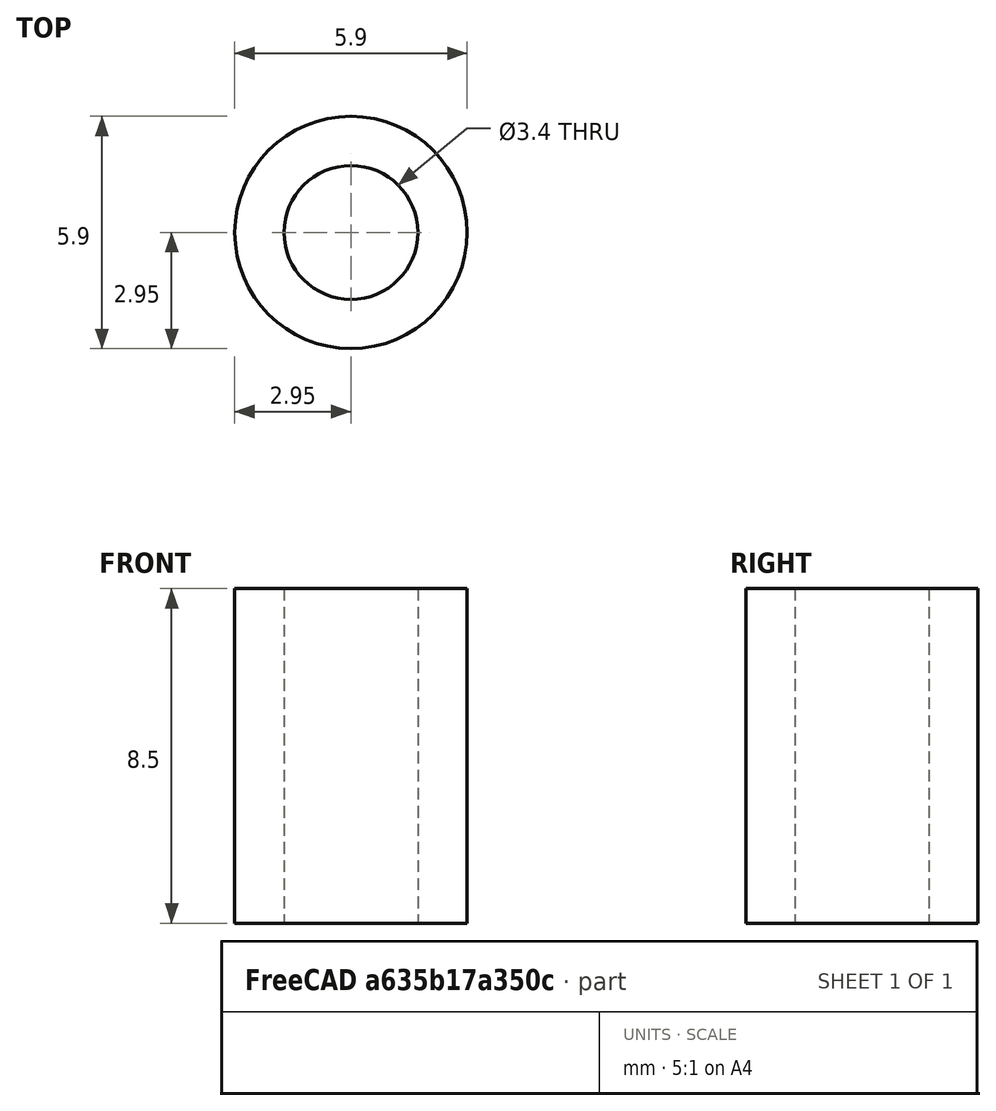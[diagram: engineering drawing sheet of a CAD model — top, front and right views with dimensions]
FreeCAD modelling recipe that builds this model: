
FCSTD DOCUMENT  (FreeCAD 2023.321R14555 (Git shallow))
Label: Spacer_9mm
License: All rights reserved
LicenseURL: http://en.wikipedia.org/wiki/All_rights_reserved
objects: Sketcher::SketchObject×1, PartDesign::Pad×1, PartDesign::Hole×1, PartDesign::Body×1, Mesh::Feature×1
note: 9 computed .brp shape members not serialized (recipe doc carries the construction recipe); baked Part::Feature solids carry a one-line shape summary decoded from their .brp

FEATURE [Sketcher::SketchObject] Sketch
  ArcFitTolerance = 1e-06
  AttachmentSupport = -> [XY_Plane]
  ExternalBSplineMaxDegree = 5
  ExternalBSplineTolerance = 0.0001
  FullyConstrained = false
  InternalTolerance = 1e-06
  InvalidShape = false
  MakeInternals = false
  MapMode = 5
  Support = -> [XY_Plane]
  TreeRank = 11
  ValidateShape = false
  sketch-geometry (1):
    g0: Circle CenterX=0 CenterY=0 CenterZ=0 NormalX=0 NormalY=0 NormalZ=1 AngleXU=0 Radius=2.9503
  constraints (1):
    c: Coincident(g0,g-1)
FEATURE [PartDesign::Pad] Pad
  AddSubType = 0
  AlongSketchNormal = false
  AutoTaperInnerAngle = true
  CheckUpToFaceLimits = true
  ClaimChildren = false
  Direction = (0,0,1)
  Fit = 0
  FitJoin = 0
  InnerFit = 0
  InnerFitJoin = 0
  InvalidShape = false
  Length = 8.5
  Length2 = 100
  Linearize = true
  NewSolid = false
  Profile = -> Sketch
  Suppress = false
  TaperInnerAngle = 0
  TaperInnerAngleRev = 0
  TreeRank = 12
  Type = 0
  ValidateShape = true
  _ProfileBasedVersion = 1
FEATURE [PartDesign::Hole] Hole
  AddSubType = 1
  BaseFeature = -> Pad
  ClaimChildren = false
  CustomThreadClearance = 0
  Depth = 25
  DepthType = 0
  Diameter = 3.4
  DrillForDepth = false
  DrillPoint = 1
  DrillPointAngle = 118
  Fit = 0
  FitJoin = 0
  HoleCutCountersinkAngle = 90
  HoleCutCustomValues = false
  HoleCutDepth = 0
  HoleCutDiameter = 6.1
  HoleCutType = 0
  InnerFit = 0
  InnerFitJoin = 0
  InvalidShape = false
  Linearize = true
  ModelThread = false
  NewSolid = false
  Profile = -> Pad [Face3]
  Suppress = false
  Tapered = false
  TaperedAngle = 90
  ThreadClass = 0
  ThreadDepth = 25
  ThreadDepthType = 0
  ThreadDirection = 0
  ThreadFit = 0
  ThreadSize = 9
  ThreadType = 1
  Threaded = false
  TreeRank = 13
  UseCustomThreadClearance = false
  ValidateShape = true
  _ProfileBasedVersion = 1
FEATURE [PartDesign::Body] Body
  AutoGroupSolids = false
  ClaimAllChildren = false
  ExportMode = 0
  Group = -> [Sketch,Pad,Hole]
  InvalidShape = false
  Origin = -> Origin
  Tip = -> Hole
  TreeRank = 10
  ValidateShape = false
  _ExportChildren = -> [Pad,Hole]
  _GroupVersion = 1
FEATURE [Mesh::Feature] Mesh  label="Hole (Meshed)"
  TreeRank = 14
